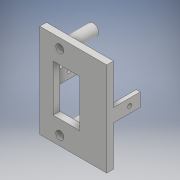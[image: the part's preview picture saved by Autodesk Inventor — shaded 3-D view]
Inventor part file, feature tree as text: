
AUTODESK INVENTOR PART (.ipt)
format: ipt  version: 2017 (Build 210142000, 142)  size: 158,720 bytes
history: native  units: mm
features: sketch x4, extrude x3, hole x1
ambient origin geometry x8: Origin, YZ Plane, XZ Plane, XY Plane, X Axis, Y Axis, Z Axis, Center Point
bodies: Solide1 (feature_tree)
feature tree (8):
  extrude  "Extrusion1"  Depth=70.0mm
  sketch  "Esquisse2"
  extrude  "Extrusion3"  Depth=50.0mm
  extrude  "Extrusion4"  Depth=15.0mm
  hole  "Perçage1"  [1 undecoded]
  sketch  "Esquisse1"
  sketch  "Esquisse3"
  sketch  "Esquisse5"
note: 1 required parameter value undecoded (feature->parameter linkage not recoverable at this tier; creation-order binding heuristic only, values carry confidence <= 0.55)
